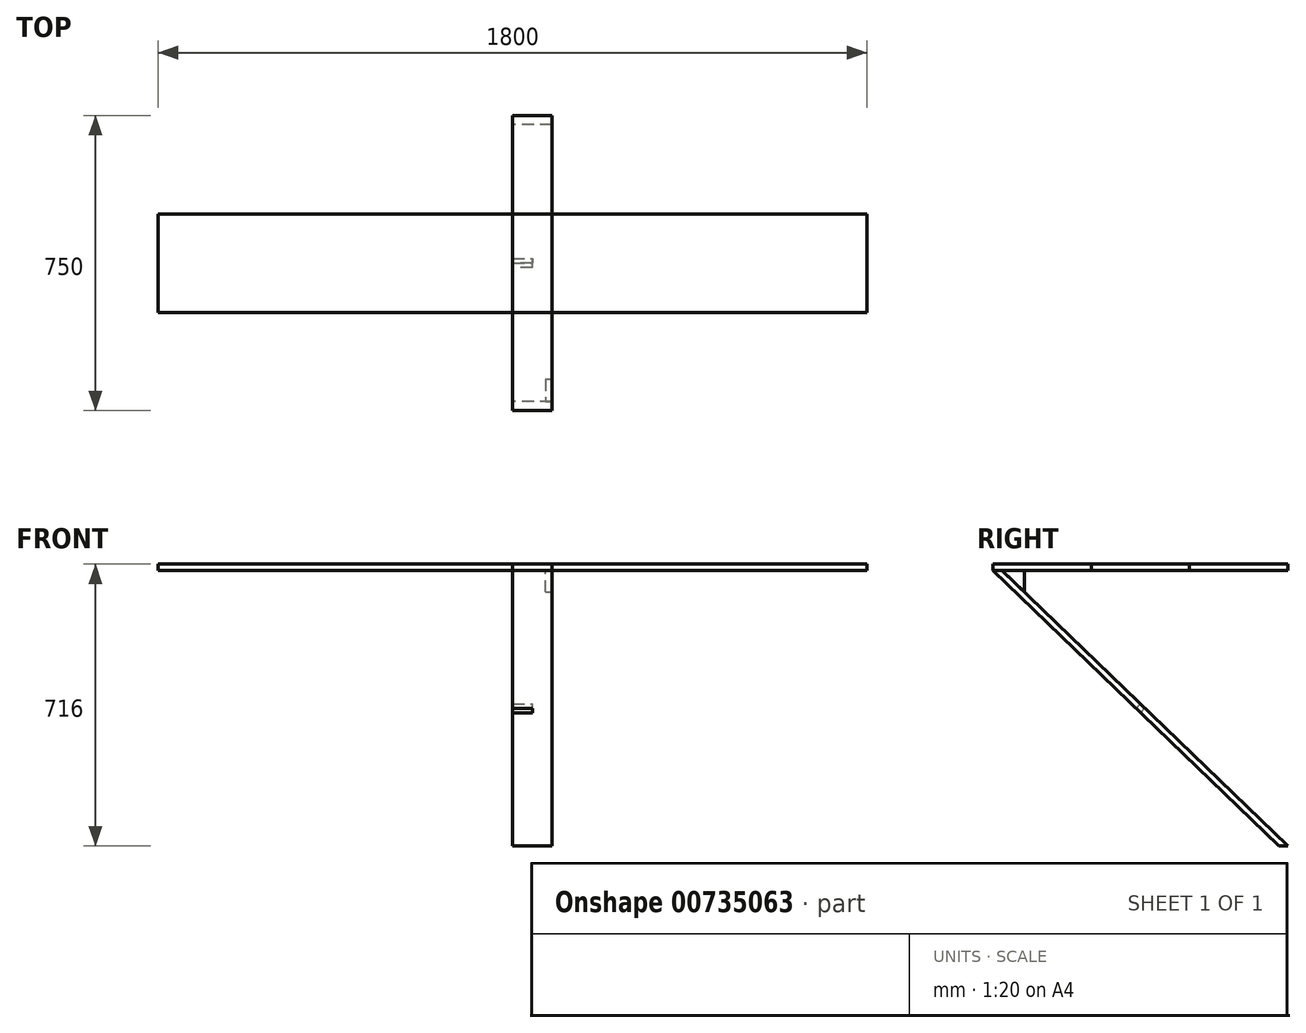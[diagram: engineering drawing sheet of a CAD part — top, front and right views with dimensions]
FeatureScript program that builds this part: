
annotation { "Feature Type Name" : "Feature", "Feature Type Description" : "" }
export const myFeature = defineFeature(function(context is Context, id is Id, definition is map)
    precondition{}
    {
        {
            var Q0;
            Q0=qCreatedBy(makeId("Top.planeOp"),FACE);
            var sketch = newSketch(context, id + "F0", { "sketchPlane" : qUnion([Q0])});
            skLineSegment(sketch, "E0.bottom", {"start": v(-900, 125) * mm, "end": v(900, 125) * mm});
            skLineSegment(sketch, "E0.top", {"start": v(-900, -125) * mm, "end": v(900, -125) * mm});
            skLineSegment(sketch, "E0.left", {"start": v(-900, 125) * mm, "end": v(-900, -125) * mm});
            skLineSegment(sketch, "E0.right", {"start": v(900, 125) * mm, "end": v(900, -125) * mm});
            skPoint(sketch, "E0.middle", {"position": v(0, 0) * mm});
            skSolve(sketch);
        }
        {
            var Q0;
            Q0=makeQuery(id+"F0.imprint","IMPRINT",FACE,{"disambiguationData":[TD([[makeQuery(id+"F0.imprint","IMPRINT",EDGE,{"derivedFrom":sQuery(id+"F0.wireOp",EDGE,"E0.bottom")}),-1.0]])]});
            extrude(context, id + "F1", {"entities" : qUnion([Q0]), "depth" : 16 * mm, "offsetDistance" : 25 * mm});
        }
        {
            var Q0;
            Q0=qCreatedBy(makeId("Right.planeOp"),FACE);
            var sketch = newSketch(context, id + "F2", { "sketchPlane" : qUnion([Q0])});
            skLineSegment(sketch, "E1", {"start": v(0, 0) * mm, "end": v(0, -700) * mm, "construction": true});
            skLineSegment(sketch, "E2.bottom", {"start": v(-375, 0) * mm, "end": v(375, 0) * mm});
            skLineSegment(sketch, "E2.top", {"start": v(-375, 16) * mm, "end": v(375, 16) * mm});
            skLineSegment(sketch, "E2.left", {"start": v(-375, 0) * mm, "end": v(-375, 16) * mm});
            skLineSegment(sketch, "E2.right", {"start": v(375, 0) * mm, "end": v(375, 16) * mm});
            skLineSegment(sketch, "E3", {"start": v(-375, 0) * mm, "end": v(351.93, -700) * mm});
            skLineSegment(sketch, "E4", {"start": v(351.93, -700) * mm, "end": v(375, -700) * mm});
            skLineSegment(sketch, "E5", {"start": v(375, -700) * mm, "end": v(-351.93, 0) * mm});
            skLineSegment(sketch, "E6", {"start": v(-351.93, 0) * mm, "end": v(-375, 0) * mm});
            skLineSegment(sketch, "E7", {"start": v(1125, -700) * mm, "end": v(-375, -700) * mm});
            skLineSegment(sketch, "E8", {"start": v(-375, -700) * mm, "end": v(-375, 1100) * mm});
            skSolve(sketch);
        }
        {
            var Q0;
            Q0=makeQuery(id+"F2.imprint","IMPRINT",FACE,{"disambiguationData":[TD([[makeQuery(id+"F2.imprint","IMPRINT",EDGE,{"derivedFrom":sQuery(id+"F2.wireOp",EDGE,"E3")}),1.0]])]});
            extrude(context, id + "F3", {"entities" : qUnion([Q0]), "depth" : 100 * mm, "offsetDistance" : 25 * mm});
        }
        {
            var Q0;
            Q0=makeQuery(id+"F3.opExtrude","SWEPT_FACE",FACE,{"disambiguationData":[OSD([sQuery(id+"F2.wireOp",EDGE,"E5")])]});
            var sketch = newSketch(context, id + "F4", { "sketchPlane" : qUnion([Q0])});
            skLineSegment(sketch, "E9.bottom", {"start": v(0, 250.77) * mm, "end": v(50, 250.77) * mm});
            skLineSegment(sketch, "E9.top", {"start": v(0, 234.77) * mm, "end": v(50, 234.77) * mm});
            skLineSegment(sketch, "E9.left", {"start": v(0, 250.77) * mm, "end": v(0, 234.77) * mm});
            skLineSegment(sketch, "E9.right", {"start": v(50, 250.77) * mm, "end": v(50, 234.77) * mm});
            skLineSegment(sketch, "E10", {"start": v(50, 242.77) * mm, "end": v(0, 242.77) * mm, "construction": true});
            skLineSegment(sketch, "E11.0", {"start": v(100, -270.12) * mm, "end": v(0, -270.12) * mm});
            skLineSegment(sketch, "E12", {"start": v(50, -270.12) * mm, "end": v(50, 755.67) * mm, "construction": true});
            skSolve(sketch);
        }
        {
            var Q0;
            Q0 = qSketchRegion(id + "F4", true);
            extrude(context, id + "F5", {"entities" : qUnion([Q0]), "operationType" : NewBodyOperationType.REMOVE, "endBound" : BoundingType.UP_TO_NEXT, "oppositeDirection" : true, "depth" : 25 * mm, "offsetDistance" : 25 * mm});
        }
        {
            var Q0;
            Q0=makeQuery(id+"F2.imprint","IMPRINT",FACE,{"disambiguationData":[TD([[makeQuery(id+"F2.imprint","IMPRINT",EDGE,{"derivedFrom":sQuery(id+"F2.wireOp",EDGE,"E2.bottom")}),1.0]])]});
            var Q1;
            Q1=makeQuery(id+"F3.opExtrude","CAP_FACE",FACE,{"disambiguationData":[OSD([sQuery(id+"F2.wireOp",EDGE,"E3"),sQuery(id+"F2.wireOp",EDGE,"E4"),sQuery(id+"F2.wireOp",EDGE,"E5"),sQuery(id+"F2.wireOp",EDGE,"E6")])],"isStart":false});
            extrude(context, id + "F6", {"entities" : qUnion([Q0]), "endBound" : BoundingType.UP_TO_SURFACE, "depth" : 25 * mm, "endBoundEntityFace" : qUnion([Q1]), "offsetDistance" : 25 * mm});
        }
        {
            var Q0;
            Q0=makeQuery(id+"F3.opExtrude","CAP_FACE",FACE,{"disambiguationData":[OSD([sQuery(id+"F2.wireOp",EDGE,"E3"),sQuery(id+"F2.wireOp",EDGE,"E4"),sQuery(id+"F2.wireOp",EDGE,"E5"),sQuery(id+"F2.wireOp",EDGE,"E6")])],"isStart":false});
            var sketch = newSketch(context, id + "F7", { "sketchPlane" : qUnion([Q0])});
            skLineSegment(sketch, "E13", {"start": v(-351.93, 0) * mm, "end": v(-294.82, -55) * mm});
            skLineSegment(sketch, "E14", {"start": v(-294.82, -55) * mm, "end": v(-294.82, 0) * mm});
            skLineSegment(sketch, "E15", {"start": v(-294.82, 0) * mm, "end": v(-351.93, 0) * mm});
            skSolve(sketch);
        }
        {
            var Q0;
            Q0=makeQuery(id+"F7.imprint","IMPRINT",FACE,{"disambiguationData":[TD([[makeQuery(id+"F7.imprint","IMPRINT",EDGE,{"derivedFrom":sQuery(id+"F7.wireOp",EDGE,"E13")}),-1.0]])]});
            extrude(context, id + "F8", {"entities" : qUnion([Q0]), "oppositeDirection" : true, "depth" : 16 * mm, "offsetDistance" : 25 * mm});
        }
        {
            var Q0;
            Q0=sQuery(id+"F2.wireOp",EDGE,"E8");
            var Q1;
            Q1=sQuery(id+"F2.wireOp",EDGE,"E7");
            extrude(context, id + "F9", {"bodyType" : ToolBodyType.SURFACE, "surfaceEntities" : qUnion([Q0, Q1]), "oppositeDirection" : true, "depth" : 3000 * mm, "offsetDistance" : 25 * mm});
        }
    });
